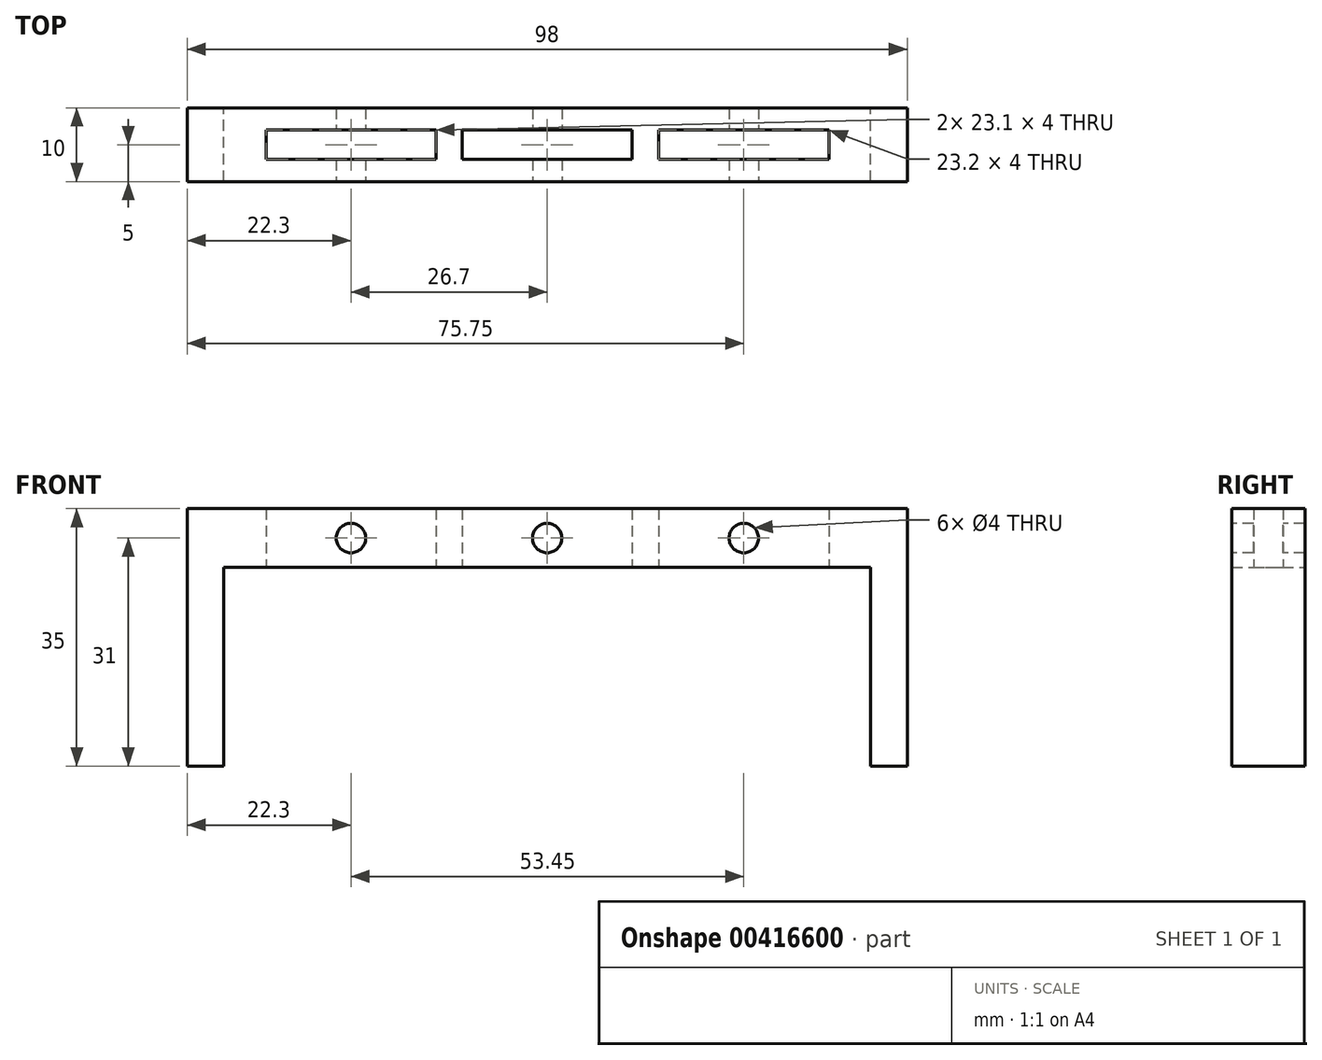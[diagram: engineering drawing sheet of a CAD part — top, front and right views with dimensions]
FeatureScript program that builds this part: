
annotation { "Feature Type Name" : "Feature", "Feature Type Description" : "" }
export const myFeature = defineFeature(function(context is Context, id is Id, definition is map)
    precondition{}
    {
        {
            var Q0;
            Q0=qCreatedBy(makeId("Front.planeOp"),FACE);
            var sketch = newSketch(context, id + "F0", { "sketchPlane" : qUnion([Q0])});
            skLineSegment(sketch, "E0.bottom", {"start": v(49, -17.5) * mm, "end": v(-49, -17.5) * mm});
            skLineSegment(sketch, "E0.top", {"start": v(49, 17.5) * mm, "end": v(-49, 17.5) * mm});
            skLineSegment(sketch, "E0.left", {"start": v(49, -17.5) * mm, "end": v(49, 17.5) * mm});
            skLineSegment(sketch, "E0.right", {"start": v(-49, -17.5) * mm, "end": v(-49, 17.5) * mm});
            skPoint(sketch, "E0.middle", {"position": v(0, 0) * mm});
            skLineSegment(sketch, "E1.bottom", {"start": v(44, -17.5) * mm, "end": v(-44, -17.5) * mm});
            skLineSegment(sketch, "E1.top", {"start": v(44, 9.5) * mm, "end": v(-44, 9.5) * mm});
            skLineSegment(sketch, "E1.left", {"start": v(44, -17.5) * mm, "end": v(44, 9.5) * mm});
            skLineSegment(sketch, "E1.right", {"start": v(-44, -17.5) * mm, "end": v(-44, 9.5) * mm});
            skPoint(sketch, "E1.middle", {"position": v(0, -4) * mm});
            skLineSegment(sketch, "E2", {"start": v(-44, -12.5) * mm, "end": v(44, -12.5) * mm});
            skSolve(sketch);
        }
        {
            var Q0;
            Q0=makeQuery(id+"F0.imprint","IMPRINT",FACE,{"disambiguationData":[TD([[makeQuery(id+"F0.imprint","IMPRINT",EDGE,{"derivedFrom":sQuery(id+"F0.wireOp",EDGE,"E0.top")}),1.0]])]});
            var Q1;
            {var subQ0=sQuery(id+"F0.wireOp",EDGE,"60aVW3nr-IxPm-GdxL-udkR-Xii73iY8wId5");Q1=makeQuery(id+"F0.imprint","IMPRINT",FACE,{"disambiguationData":[TD([[makeQuery(id+"F0.imprint","IMPRINT",EDGE,{"derivedFrom":subQ0}),1.0]])]});}
            var Q2;
            {var subQ3=sQuery(id+"F0.wireOp",EDGE,"D7AiWPTI-Wj8n-tMTe-JRpB-ptFEJoSc7qR4");Q2=makeQuery(id+"F0.imprint","IMPRINT",FACE,{"disambiguationData":[TD([[makeQuery(id+"F0.imprint","IMPRINT",EDGE,{"derivedFrom":subQ3}),-1.0]])]});}
            var Q3;
            {var subQ0=sQuery(id+"F0.wireOp",EDGE,"E1.bottom");Q3=makeQuery(id+"F0.imprint","IMPRINT",FACE,{"disambiguationData":[TD([[makeQuery(id+"F0.imprint","IMPRINT",EDGE,{"derivedFrom":subQ0}),-1.0]])]});}
            extrude(context, id + "F1", {"entities" : qUnion([Q0, Q1, Q2, Q3]), "endBound" : BoundingType.SYMMETRIC, "depth" : 10 * mm});
        }
        {
            var Q0;
            Q0=qCreatedBy(makeId("Top.planeOp"),FACE);
            var sketch = newSketch(context, id + "F2", { "sketchPlane" : qUnion([Q0])});
            skLineSegment(sketch, "E3.bottom", {"start": v(-15.15, -2) * mm, "end": v(-38.25, -2) * mm});
            skLineSegment(sketch, "E3.top", {"start": v(-15.15, 2) * mm, "end": v(-38.25, 2) * mm});
            skLineSegment(sketch, "E3.left", {"start": v(-15.15, -2) * mm, "end": v(-15.15, 2) * mm});
            skLineSegment(sketch, "E3.right", {"start": v(-38.25, -2) * mm, "end": v(-38.25, 2) * mm});
            skPoint(sketch, "E3.middle", {"position": v(-26.7, 0) * mm});
            skLineSegment(sketch, "E4.bottom", {"start": v(11.55, -2) * mm, "end": v(-11.55, -2) * mm});
            skLineSegment(sketch, "E4.top", {"start": v(11.55, 2) * mm, "end": v(-11.55, 2) * mm});
            skLineSegment(sketch, "E4.left", {"start": v(11.55, -2) * mm, "end": v(11.55, 2) * mm});
            skLineSegment(sketch, "E4.right", {"start": v(-11.55, -2) * mm, "end": v(-11.55, 2) * mm});
            skPoint(sketch, "E4.middle", {"position": v(0, 0) * mm});
            skLineSegment(sketch, "E5.bottom", {"start": v(38.35, -2) * mm, "end": v(15.15, -2) * mm});
            skLineSegment(sketch, "E5.top", {"start": v(38.35, 2) * mm, "end": v(15.15, 2) * mm});
            skLineSegment(sketch, "E5.left", {"start": v(38.35, -2) * mm, "end": v(38.35, 2) * mm});
            skLineSegment(sketch, "E5.right", {"start": v(15.15, -2) * mm, "end": v(15.15, 2) * mm});
            skPoint(sketch, "E5.middle", {"position": v(26.75, 0) * mm});
            skSolve(sketch);
        }
        {
            var Q0;
            Q0=makeQuery(id+"F2.imprint","IMPRINT",FACE,{"disambiguationData":[TD([[makeQuery(id+"F2.imprint","IMPRINT",EDGE,{"derivedFrom":sQuery(id+"F2.wireOp",EDGE,"E3.bottom")}),-1.0]])]});
            var Q1;
            Q1=makeQuery(id+"F2.imprint","IMPRINT",FACE,{"disambiguationData":[TD([[makeQuery(id+"F2.imprint","IMPRINT",EDGE,{"derivedFrom":sQuery(id+"F2.wireOp",EDGE,"E4.bottom")}),-1.0]])]});
            var Q2;
            Q2=makeQuery(id+"F2.imprint","IMPRINT",FACE,{"disambiguationData":[TD([[makeQuery(id+"F2.imprint","IMPRINT",EDGE,{"derivedFrom":sQuery(id+"F2.wireOp",EDGE,"E5.bottom")}),-1.0]])]});
            extrude(context, id + "F3", {"entities" : qUnion([Q0, Q1, Q2]), "operationType" : NewBodyOperationType.REMOVE, "endBound" : BoundingType.THROUGH_ALL, "depth" : 17.4 * mm});
        }
        {
            var Q0;
            Q0=makeQuery(id+"F1.opExtrude","CAP_FACE",FACE,{"disambiguationData":[OSD([sQuery(id+"F0.wireOp",EDGE,"E0.bottom"),sQuery(id+"F0.wireOp",EDGE,"E0.top"),sQuery(id+"F0.wireOp",EDGE,"E0.left"),sQuery(id+"F0.wireOp",EDGE,"E0.right"),sQuery(id+"F0.wireOp",EDGE,"E1.bottom"),sQuery(id+"F0.wireOp",EDGE,"E1.top"),sQuery(id+"F0.wireOp",EDGE,"E1.left"),sQuery(id+"F0.wireOp",EDGE,"E1.right"),sQuery(id+"F0.wireOp",EDGE,"60aVW3nr-IxPm-GdxL-udkR-Xii73iY8wId5"),sQuery(id+"F0.wireOp",EDGE,"E2")])],"isStart":false});
            var sketch = newSketch(context, id + "F4", { "sketchPlane" : qUnion([Q0])});
            skLineSegment(sketch, "E6", {"start": v(-26.7, 9.5) * mm, "end": v(-26.7, 17.5) * mm});
            skLineSegment(sketch, "E7.0", {"start": v(49, 17.5) * mm, "end": v(-49, 17.5) * mm});
            skLineSegment(sketch, "E8", {"start": v(0, 9.5) * mm, "end": v(0, 17.5) * mm});
            skLineSegment(sketch, "E9", {"start": v(26.75, 9.5) * mm, "end": v(26.75, 17.5) * mm});
            skCircle(sketch, "E10", {"center": v(-26.7, 13.5) * mm, "radius": 2 * mm});
            skCircle(sketch, "E11", {"center": v(0, 13.5) * mm, "radius": 2 * mm});
            skCircle(sketch, "E12", {"center": v(26.75, 13.5) * mm, "radius": 2 * mm});
            skSolve(sketch);
        }
        {
            var Q0;
            {var subQ0=sQuery(id+"F4.wireOp",EDGE,"E10");var subQ1=sQuery(id+"F4.wireOp",EDGE,"E6");var subQ2=makeQuery(id+"F4.imprint","INTERSECT",VERTEX,{"disambiguationData":[OD(0.0)],"derivedFrom":[subQ1,subQ0]});Q0=makeQuery(id+"F4.imprint","IMPRINT",FACE,{"disambiguationData":[TD([[makeQuery(id+"F4.imprint","IMPRINT",EDGE,{"disambiguationData":[TD([[subQ2,-1.0]])],"derivedFrom":subQ1}),1.0]])]});}
            var Q1;
            {var subQ0=sQuery(id+"F4.wireOp",EDGE,"E10");var subQ1=sQuery(id+"F4.wireOp",EDGE,"E6");var subQ2=makeQuery(id+"F4.imprint","INTERSECT",VERTEX,{"disambiguationData":[OD(0.0)],"derivedFrom":[subQ1,subQ0]});Q1=makeQuery(id+"F4.imprint","IMPRINT",FACE,{"disambiguationData":[TD([[makeQuery(id+"F4.imprint","IMPRINT",EDGE,{"disambiguationData":[TD([[subQ2,-1.0]])],"derivedFrom":subQ1}),-1.0]])]});}
            var Q2;
            {var subQ0=sQuery(id+"F4.wireOp",EDGE,"E11");var subQ1=sQuery(id+"F4.wireOp",EDGE,"E8");var subQ2=makeQuery(id+"F4.imprint","INTERSECT",VERTEX,{"disambiguationData":[OD(0.0)],"derivedFrom":[subQ1,subQ0]});Q2=makeQuery(id+"F4.imprint","IMPRINT",FACE,{"disambiguationData":[TD([[makeQuery(id+"F4.imprint","IMPRINT",EDGE,{"disambiguationData":[TD([[subQ2,-1.0]])],"derivedFrom":subQ1}),1.0]])]});}
            var Q3;
            {var subQ0=sQuery(id+"F4.wireOp",EDGE,"E11");var subQ1=sQuery(id+"F4.wireOp",EDGE,"E8");var subQ2=makeQuery(id+"F4.imprint","INTERSECT",VERTEX,{"disambiguationData":[OD(0.0)],"derivedFrom":[subQ1,subQ0]});Q3=makeQuery(id+"F4.imprint","IMPRINT",FACE,{"disambiguationData":[TD([[makeQuery(id+"F4.imprint","IMPRINT",EDGE,{"disambiguationData":[TD([[subQ2,-1.0]])],"derivedFrom":subQ1}),-1.0]])]});}
            var Q4;
            {var subQ0=sQuery(id+"F4.wireOp",EDGE,"E12");var subQ1=sQuery(id+"F4.wireOp",EDGE,"E9");var subQ2=makeQuery(id+"F4.imprint","INTERSECT",VERTEX,{"disambiguationData":[OD(0.0)],"derivedFrom":[subQ1,subQ0]});Q4=makeQuery(id+"F4.imprint","IMPRINT",FACE,{"disambiguationData":[TD([[makeQuery(id+"F4.imprint","IMPRINT",EDGE,{"disambiguationData":[TD([[subQ2,-1.0]])],"derivedFrom":subQ1}),1.0]])]});}
            var Q5;
            {var subQ0=sQuery(id+"F4.wireOp",EDGE,"E12");var subQ1=sQuery(id+"F4.wireOp",EDGE,"E9");var subQ2=makeQuery(id+"F4.imprint","INTERSECT",VERTEX,{"disambiguationData":[OD(0.0)],"derivedFrom":[subQ1,subQ0]});Q5=makeQuery(id+"F4.imprint","IMPRINT",FACE,{"disambiguationData":[TD([[makeQuery(id+"F4.imprint","IMPRINT",EDGE,{"disambiguationData":[TD([[subQ2,-1.0]])],"derivedFrom":subQ1}),-1.0]])]});}
            extrude(context, id + "F5", {"entities" : qUnion([Q0, Q1, Q2, Q3, Q4, Q5]), "operationType" : NewBodyOperationType.REMOVE, "endBound" : BoundingType.THROUGH_ALL, "oppositeDirection" : true, "depth" : 25 * mm});
        }
    });
